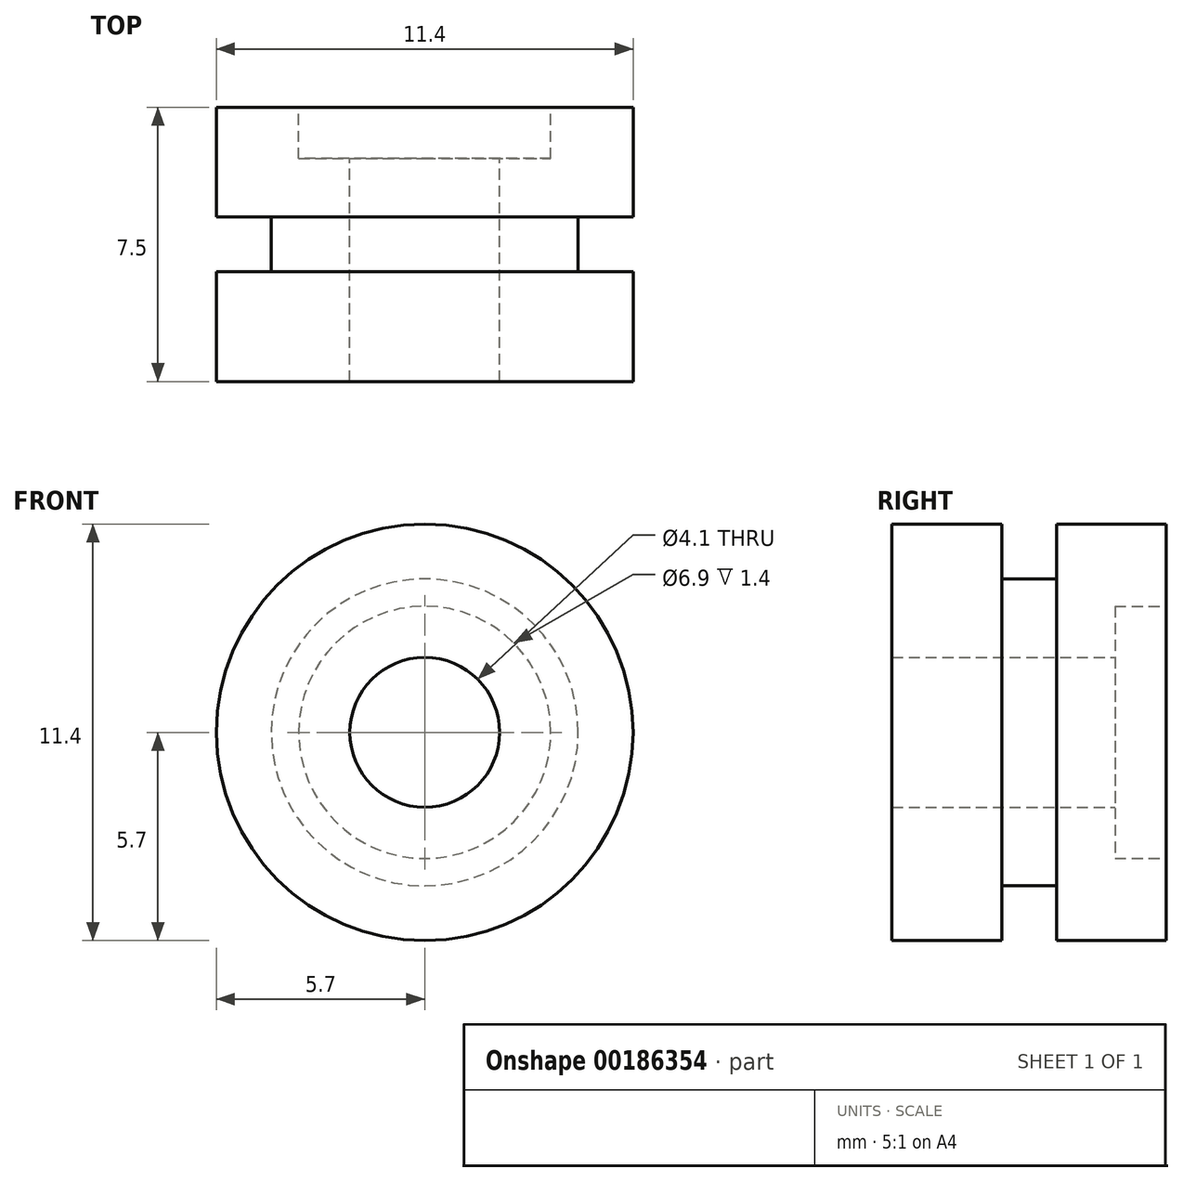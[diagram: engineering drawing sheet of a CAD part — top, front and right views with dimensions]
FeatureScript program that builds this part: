
annotation { "Feature Type Name" : "Feature", "Feature Type Description" : "" }
export const myFeature = defineFeature(function(context is Context, id is Id, definition is map)
    precondition{}
    {
        {
            var Q0;
            Q0=qCreatedBy(makeId("Right.planeOp"),FACE);
            var sketch = newSketch(context, id + "F0", { "sketchPlane" : qUnion([Q0])});
            skLineSegment(sketch, "E0", {"start": v(11.47, 0) * mm, "end": v(0, 0) * mm, "construction": true});
            skLineSegment(sketch, "E1", {"start": v(6.1, 2.05) * mm, "end": v(0, 2.05) * mm});
            skLineSegment(sketch, "E2", {"start": v(6.1, 2.05) * mm, "end": v(6.1, 3.45) * mm});
            skLineSegment(sketch, "E3", {"start": v(7.5, 3.45) * mm, "end": v(6.1, 3.45) * mm});
            skLineSegment(sketch, "E4", {"start": v(7.5, 3.45) * mm, "end": v(7.5, 5.7) * mm});
            skLineSegment(sketch, "E5", {"start": v(4.5, 5.7) * mm, "end": v(7.5, 5.7) * mm});
            skLineSegment(sketch, "E6", {"start": v(4.5, 5.7) * mm, "end": v(4.5, 4.2) * mm});
            skLineSegment(sketch, "E7", {"start": v(3, 4.2) * mm, "end": v(4.5, 4.2) * mm});
            skLineSegment(sketch, "E8", {"start": v(3, 4.2) * mm, "end": v(3, 5.7) * mm});
            skLineSegment(sketch, "E9", {"start": v(0, 5.7) * mm, "end": v(3, 5.7) * mm});
            skLineSegment(sketch, "E10", {"start": v(0, 5.7) * mm, "end": v(0, 2.05) * mm});
            skLineSegment(sketch, "E11", {"start": v(4.5, 4.2) * mm, "end": v(4.5, 5.7) * mm});
            skLineSegment(sketch, "E12", {"start": v(3, 5.7) * mm, "end": v(4.5, 5.7) * mm});
            skLineSegment(sketch, "E13", {"start": v(3, 5.7) * mm, "end": v(3, 4.2) * mm});
            skLineSegment(sketch, "E14.trimOffspring", {"start": v(4.5, 4.2) * mm, "end": v(3, 4.2) * mm});
            skSolve(sketch);
        }
        {
            var Q0;
            Q0=makeQuery(id+"F0.imprint","IMPRINT",FACE,{"disambiguationData":[TD([[makeQuery(id+"F0.imprint","IMPRINT",EDGE,{"derivedFrom":sQuery(id+"F0.wireOp",EDGE,"E1")}),-1.0]])]});
            var Q1;
            Q1=sQuery(id+"F0.wireOp",EDGE,"E0");
            revolve(context, id + "F1", {"entities" : qUnion([Q0]), "axis" : qUnion([Q1]), "revolveType" : RevolveType.FULL});
        }
    });
